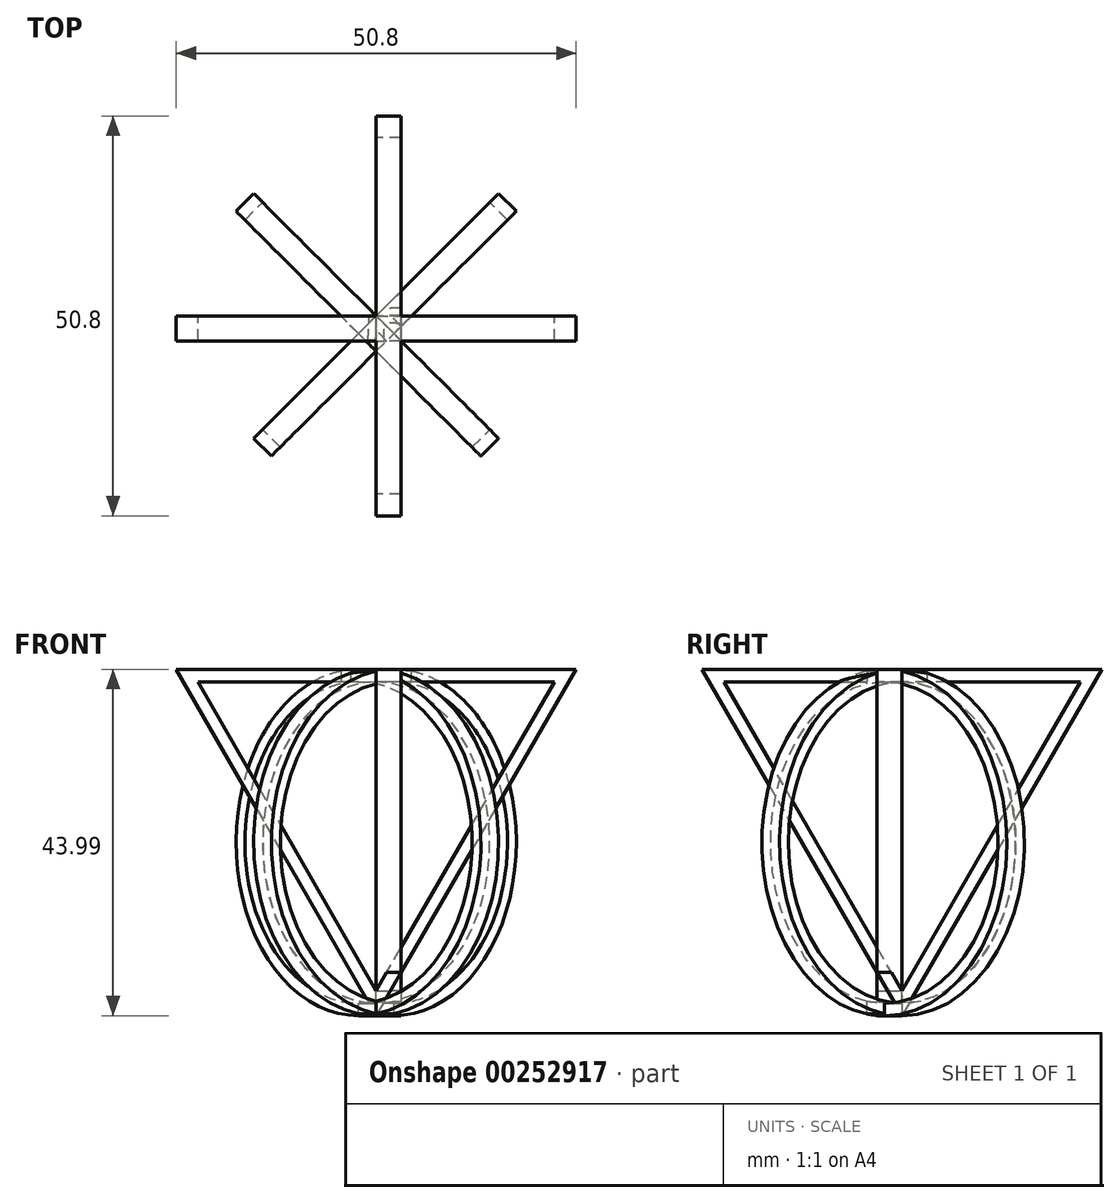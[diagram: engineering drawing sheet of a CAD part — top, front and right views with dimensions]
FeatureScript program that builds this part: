
annotation { "Feature Type Name" : "Feature", "Feature Type Description" : "" }
export const myFeature = defineFeature(function(context is Context, id is Id, definition is map)
    precondition{}
    {
        {
            var Q0;
            Q0=qCreatedBy(makeId("Front.planeOp"),FACE);
            var sketch = newSketch(context, id + "F0", { "sketchPlane" : qUnion([Q0])});
            skLineSegment(sketch, "E0", {"start": v(0, 0) * mm, "end": v(25.4, 0) * mm});
            skLineSegment(sketch, "E1", {"start": v(0, 0) * mm, "end": v(-25.4, 0) * mm});
            skLineSegment(sketch, "E2", {"start": v(-25.4, 0) * mm, "end": v(0, -44) * mm});
            skLineSegment(sketch, "E3", {"start": v(25.4, 0) * mm, "end": v(0, -44) * mm});
            skLineSegment(sketch, "E4", {"start": v(-16.12, -12.9) * mm, "end": v(-22.65, -1.59) * mm});
            skLineSegment(sketch, "E5", {"start": v(-22.65, -1.59) * mm, "end": v(0, -40.82) * mm});
            skLineSegment(sketch, "E6", {"start": v(5.18, -31.85) * mm, "end": v(22.65, -1.59) * mm});
            skLineSegment(sketch, "E7", {"start": v(22.65, -1.59) * mm, "end": v(0, -40.82) * mm});
            skLineSegment(sketch, "E8", {"start": v(22.65, -1.59) * mm, "end": v(-22.65, -1.59) * mm});
            skPoint(sketch, "E9.end.orphan", {"position": v(-1.96, -1.59) * mm});
            skPoint(sketch, "E10.orphan", {"position": v(23.57, 0) * mm});
            skSolve(sketch);
        }
        {
            var Q0;
            Q0=qCreatedBy(makeId("Right.planeOp"),FACE);
            var sketch = newSketch(context, id + "F1", { "sketchPlane" : qUnion([Q0])});
            skLineSegment(sketch, "E11", {"start": v(0, 0) * mm, "end": v(25.4, 0) * mm});
            skLineSegment(sketch, "E12", {"start": v(0, 0) * mm, "end": v(-25.4, 0) * mm});
            skLineSegment(sketch, "E13", {"start": v(-25.4, 0) * mm, "end": v(0, -44) * mm});
            skLineSegment(sketch, "E14", {"start": v(25.4, 0) * mm, "end": v(0, -44) * mm});
            skLineSegment(sketch, "E15", {"start": v(4.38, -1.59) * mm, "end": v(-22.65, -1.59) * mm});
            skLineSegment(sketch, "E16", {"start": v(-22.65, -1.59) * mm, "end": v(22.65, -1.59) * mm});
            skLineSegment(sketch, "E17", {"start": v(16.1, -12.94) * mm, "end": v(22.65, -1.59) * mm});
            skLineSegment(sketch, "E18", {"start": v(22.65, -1.59) * mm, "end": v(0, -40.82) * mm});
            skLineSegment(sketch, "E19", {"start": v(0, -40.82) * mm, "end": v(-22.65, -1.59) * mm});
            skSolve(sketch);
        }
        {
            var Q0;
            Q0=sQuery(id+"F1.wireOp",EDGE,"E11");
            cPlane(context, id + "F2", {"entities" : qUnion([Q0]), "cplaneType" : CPlaneType.LINE_ANGLE, "offset" : 25.4 * mm, "angle" : 0 * degree, "width" : 152.4 * mm, "height" : 152.4 * mm});
        }
        {
            var Q0;
            Q0=qCreatedBy(id+"F2.planeOp",FACE);
            var sketch = newSketch(context, id + "F3", { "sketchPlane" : qUnion([Q0])});
            skLineSegment(sketch, "E20.0", {"start": v(0, 0) * mm, "end": v(0, 25.4) * mm});
            skLineSegment(sketch, "E21", {"start": v(0, 0) * mm, "end": v(-17.68, 17.68) * mm});
            skLineSegment(sketch, "E22", {"start": v(0, 0) * mm, "end": v(13.72, 13.72) * mm});
            skSolve(sketch);
        }
        {
            var Q0;
            Q0=sQuery(id+"F3.wireOp",EDGE,"E21");
            var Q1;
            Q1=sQuery(id+"F3.wireOp",EDGE,"E20.0");
            cPlane(context, id + "F4", {"entities" : qUnion([Q0, Q1]), "cplaneType" : CPlaneType.LINE_ANGLE, "offset" : 25.4 * mm, "angle" : 90 * degree, "width" : 152.4 * mm, "height" : 152.4 * mm});
        }
        {
            var Q0;
            Q0=qCreatedBy(id+"F4.planeOp",FACE);
            var sketch = newSketch(context, id + "F5", { "sketchPlane" : qUnion([Q0])});
            skCircle(sketch, "E23", {"center": v(0, -22) * mm, "radius": 22 * mm});
            skCircle(sketch, "E24", {"center": v(0, -22) * mm, "radius": 20.4 * mm});
            skSolve(sketch);
        }
        {
            var Q0;
            Q0=sQuery(id+"F3.wireOp",EDGE,"E22");
            var Q1;
            Q1=sQuery(id+"F3.wireOp",EDGE,"E20.0");
            cPlane(context, id + "F6", {"entities" : qUnion([Q0, Q1]), "cplaneType" : CPlaneType.LINE_ANGLE, "offset" : 25.4 * mm, "angle" : 90 * degree, "width" : 152.4 * mm, "height" : 152.4 * mm});
        }
        {
            var Q0;
            Q0=qCreatedBy(id+"F6.planeOp",FACE);
            var sketch = newSketch(context, id + "F7", { "sketchPlane" : qUnion([Q0])});
            skCircle(sketch, "E25", {"center": v(0, -22) * mm, "radius": 22 * mm});
            skCircle(sketch, "E26", {"center": v(0, -22) * mm, "radius": 20.4 * mm});
            skSolve(sketch);
        }
        {
            var Q0;
            Q0 = qSketchRegion(id + "F0", true);
            extrude(context, id + "F8", {"entities" : qUnion([Q0]), "depth" : 3.17 * mm});
        }
        {
            var Q0;
            Q0=makeQuery(id+"F1.imprint","IMPRINT",FACE,{"disambiguationData":[TD([[makeQuery(id+"F1.imprint","IMPRINT",EDGE,{"derivedFrom":sQuery(id+"F1.wireOp",EDGE,"E11")}),-1.0]])]});
            extrude(context, id + "F9", {"entities" : qUnion([Q0]), "operationType" : NewBodyOperationType.ADD, "depth" : 3.17 * mm});
        }
        {
            var Q0;
            Q0=makeQuery(id+"F5.imprint","IMPRINT",FACE,{"disambiguationData":[TD([[makeQuery(id+"F5.imprint","IMPRINT",EDGE,{"derivedFrom":sQuery(id+"F5.wireOp",EDGE,"E23")}),1.0]])]});
            extrude(context, id + "F10", {"entities" : qUnion([Q0]), "operationType" : NewBodyOperationType.ADD, "depth" : 3.17 * mm});
        }
        {
            var Q0;
            Q0=makeQuery(id+"F7.imprint","IMPRINT",FACE,{"disambiguationData":[TD([[makeQuery(id+"F7.imprint","IMPRINT",EDGE,{"derivedFrom":sQuery(id+"F7.wireOp",EDGE,"E25")}),1.0]])]});
            extrude(context, id + "F11", {"entities" : qUnion([Q0]), "operationType" : NewBodyOperationType.ADD, "depth" : 3.17 * mm});
        }
    });
